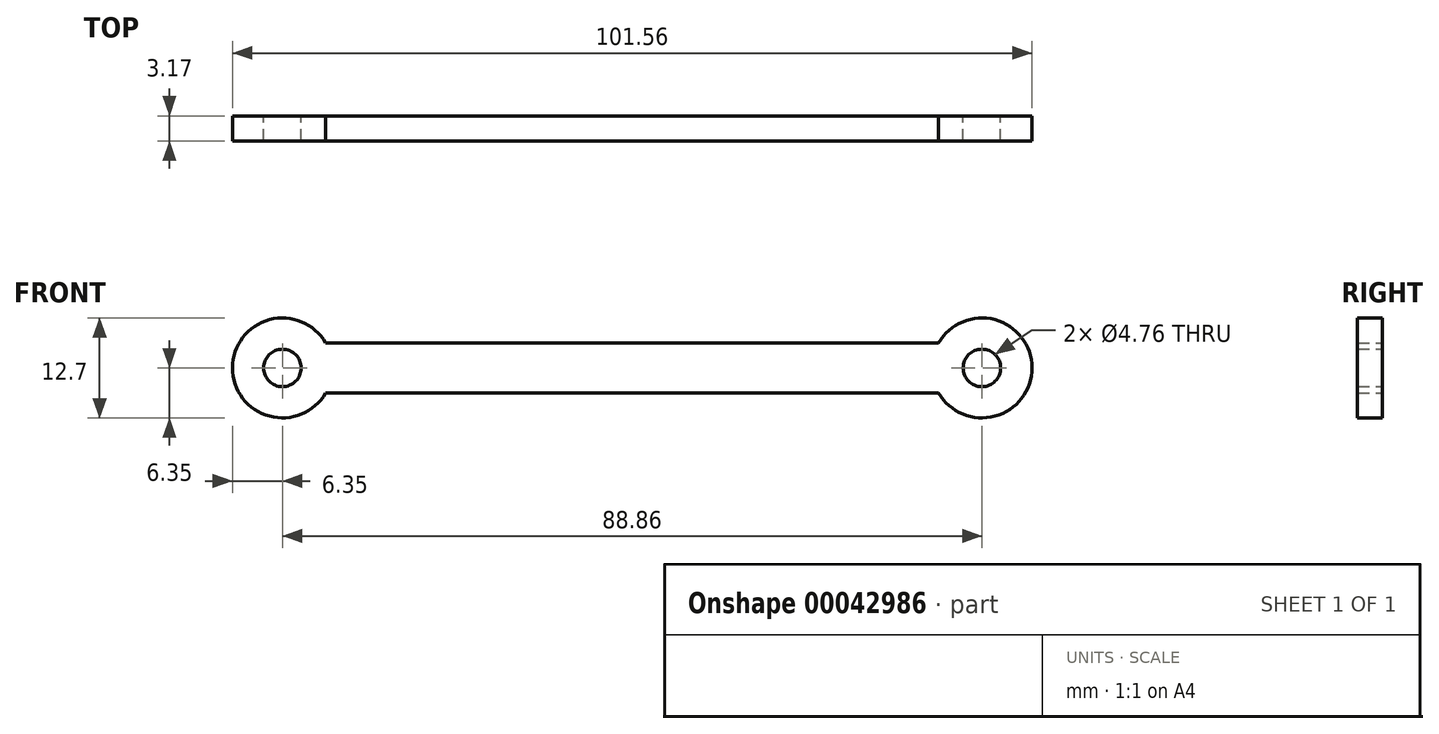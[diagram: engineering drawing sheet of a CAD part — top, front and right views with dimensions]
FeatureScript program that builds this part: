
annotation { "Feature Type Name" : "Feature", "Feature Type Description" : "" }
export const myFeature = defineFeature(function(context is Context, id is Id, definition is map)
    precondition{}
    {
        {
            var Q0;
            Q0=qCreatedBy(makeId("Front.planeOp"),FACE);
            var sketch = newSketch(context, id + "F0", { "sketchPlane" : qUnion([Q0])});
            skLineSegment(sketch, "E0.bottom", {"start": v(-42.67, 6.6) * mm, "end": v(46.23, 6.6) * mm});
            skLineSegment(sketch, "E0.top", {"start": v(-42.67, 0.25) * mm, "end": v(46.23, 0.25) * mm});
            skLineSegment(sketch, "E0.left", {"start": v(-42.67, 6.6) * mm, "end": v(-42.67, 0.25) * mm});
            skLineSegment(sketch, "E0.right", {"start": v(46.23, 6.6) * mm, "end": v(46.23, 0.25) * mm});
            skCircle(sketch, "E1", {"center": v(46.19, 3.43) * mm, "radius": 6.35 * mm});
            skCircle(sketch, "E2", {"center": v(-42.67, 3.43) * mm, "radius": 6.35 * mm});
            skSolve(sketch);
        }
        {
            var Q0;
            {var subQ0=sQuery(id+"F0.wireOp",EDGE,"E2");var subQ3=sQuery(id+"F0.wireOp",EDGE,"E0.bottom");var subQ4=makeQuery(id+"F0.imprint","INTERSECT",VERTEX,{"derivedFrom":[subQ3,subQ0]});Q0=makeQuery(id+"F0.imprint","IMPRINT",FACE,{"disambiguationData":[TD([[makeQuery(id+"F0.imprint","IMPRINT",EDGE,{"disambiguationData":[TD([[subQ4,-1.0]])],"derivedFrom":subQ3}),-1.0]])]});}
            var Q1;
            {var subQ5=sQuery(id+"F0.wireOp",EDGE,"E0.left");Q1=makeQuery(id+"F0.imprint","IMPRINT",FACE,{"disambiguationData":[TD([[makeQuery(id+"F0.imprint","IMPRINT",EDGE,{"derivedFrom":subQ5}),1.0]])]});}
            var Q2;
            {var subQ5=sQuery(id+"F0.wireOp",EDGE,"E0.left");Q2=makeQuery(id+"F0.imprint","IMPRINT",FACE,{"disambiguationData":[TD([[makeQuery(id+"F0.imprint","IMPRINT",EDGE,{"derivedFrom":subQ5}),-1.0]])]});}
            var Q3;
            {var subQ5=sQuery(id+"F0.wireOp",EDGE,"E0.right");Q3=makeQuery(id+"F0.imprint","IMPRINT",FACE,{"disambiguationData":[TD([[makeQuery(id+"F0.imprint","IMPRINT",EDGE,{"derivedFrom":subQ5}),1.0]])]});}
            var Q4;
            {var subQ5=sQuery(id+"F0.wireOp",EDGE,"E0.right");Q4=makeQuery(id+"F0.imprint","IMPRINT",FACE,{"disambiguationData":[TD([[makeQuery(id+"F0.imprint","IMPRINT",EDGE,{"derivedFrom":subQ5}),-1.0]])]});}
            extrude(context, id + "F1", {"entities" : qUnion([Q0, Q1, Q2, Q3, Q4]), "depth" : 3.17 * mm});
        }
        {
            var Q0;
            Q0=sQuery(id+"F0.wireOp",VERTEX,"E2.center");
            var Q1;
            Q1=makeQuery(id+"F1.opExtrude","SWEPT_BODY",BODY,{"disambiguationData":[OSD([sQuery(id+"F0.wireOp",EDGE,"E0.bottom"),sQuery(id+"F0.wireOp",EDGE,"E0.top"),sQuery(id+"F0.wireOp",EDGE,"E1"),sQuery(id+"F0.wireOp",EDGE,"E2")])]});
            hole(context, id + "F2", {"style" : HoleStyle.SIMPLE, "holeDiameter" : 4.76 * mm, "endStyle" : HoleEndStyle.THROUGH, "oppositeDirection" : true, "locations" : qUnion([Q0]), "scope" : qUnion([Q1])});
        }
        {
            var Q0;
            Q0=sQuery(id+"F0.wireOp",VERTEX,"E1.center");
            var Q1;
            Q1=makeQuery(id+"F1.opExtrude","SWEPT_BODY",BODY,{"disambiguationData":[OSD([sQuery(id+"F0.wireOp",EDGE,"E0.bottom"),sQuery(id+"F0.wireOp",EDGE,"E0.top"),sQuery(id+"F0.wireOp",EDGE,"E1"),sQuery(id+"F0.wireOp",EDGE,"E2")])]});
            hole(context, id + "F3", {"style" : HoleStyle.SIMPLE, "holeDiameter" : 4.76 * mm, "endStyle" : HoleEndStyle.THROUGH, "oppositeDirection" : true, "locations" : qUnion([Q0]), "scope" : qUnion([Q1])});
        }
    });
